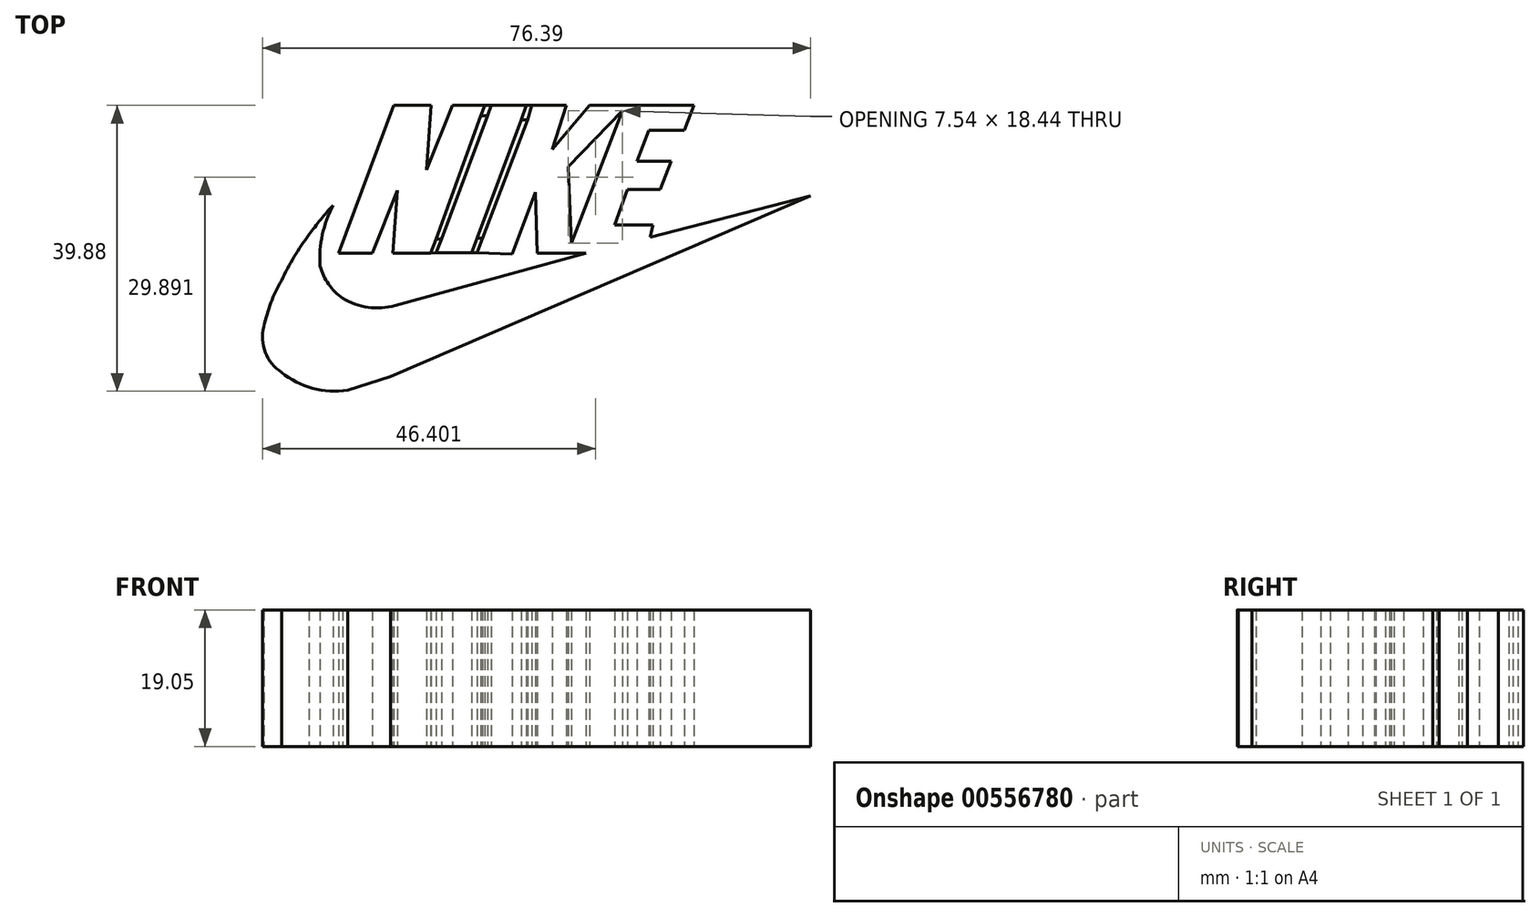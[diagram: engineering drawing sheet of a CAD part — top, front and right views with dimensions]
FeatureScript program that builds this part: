
annotation { "Feature Type Name" : "Feature", "Feature Type Description" : "" }
export const myFeature = defineFeature(function(context is Context, id is Id, definition is map)
    precondition{}
    {
        {
            var Q0;
            Q0=qCreatedBy(makeId("Top.planeOp"),FACE);
            var sketch = newSketch(context, id + "F0", { "sketchPlane" : qUnion([Q0])});
            skLineSegment(sketch, "E0", {"start": v(-58.07, 39.74) * mm, "end": v(-65.82, 19.1) * mm});
            skLineSegment(sketch, "E1", {"start": v(-65.82, 19.1) * mm, "end": v(-61.07, 19.1) * mm});
            skLineSegment(sketch, "E2", {"start": v(-61.07, 19.1) * mm, "end": v(-57.6, 27.87) * mm});
            skLineSegment(sketch, "E3", {"start": v(-57.6, 27.87) * mm, "end": v(-58.23, 19.1) * mm});
            skLineSegment(sketch, "E4", {"start": v(-58.23, 19.1) * mm, "end": v(-52.94, 19.1) * mm});
            skLineSegment(sketch, "E5", {"start": v(-45.41, 39.74) * mm, "end": v(-49.94, 39.74) * mm});
            skLineSegment(sketch, "E6", {"start": v(-49.94, 39.74) * mm, "end": v(-53.5, 30.77) * mm});
            skLineSegment(sketch, "E7", {"start": v(-53.5, 30.77) * mm, "end": v(-52.88, 39.74) * mm});
            skLineSegment(sketch, "E8", {"start": v(-52.88, 39.74) * mm, "end": v(-58.07, 39.74) * mm});
            skLineSegment(sketch, "E9", {"start": v(-44.5, 39.74) * mm, "end": v(-39.63, 39.74) * mm});
            skLineSegment(sketch, "E10", {"start": v(-52.2, 19.19) * mm, "end": v(-47.26, 19.19) * mm});
            skLineSegment(sketch, "E11", {"start": v(-38.37, 27.66) * mm, "end": v(-41.6, 18.98) * mm});
            skLineSegment(sketch, "E12", {"start": v(-41.6, 18.98) * mm, "end": v(-46.5, 19.19) * mm});
            skLineSegment(sketch, "E13", {"start": v(-38.12, 19.1) * mm, "end": v(-38.37, 27.66) * mm});
            skLineSegment(sketch, "E14", {"start": v(-31.33, 19.1) * mm, "end": v(-38.12, 19.1) * mm});
            skLineSegment(sketch, "E15", {"start": v(-31.33, 19.1) * mm, "end": v(-57.9, 11.81) * mm});
            skArc(sketch, "E16", {"start": v(-65.2, 12.82) * mm, "mid": v(-61.66, 11.57) * mm, "end": v(-57.9, 11.81) * mm});
            skArc(sketch, "E17", {"start": v(-68.38, 17.34) * mm, "mid": v(-67.18, 14.8) * mm, "end": v(-65.2, 12.82) * mm});
            skArc(sketch, "E18", {"start": v(-66.54, 25.81) * mm, "mid": v(-68.04, 21.7) * mm, "end": v(-68.38, 17.34) * mm});
            skArc(sketch, "E19", {"start": v(-66.54, 25.81) * mm, "mid": v(-68.29, 23.82) * mm, "end": v(-69.9, 21.7) * mm});
            skArc(sketch, "E20", {"start": v(-69.9, 21.7) * mm, "mid": v(-71.98, 18.61) * mm, "end": v(-73.75, 15.33) * mm});
            skArc(sketch, "E21", {"start": v(-73.75, 15.33) * mm, "mid": v(-75.23, 12.2) * mm, "end": v(-76.2, 8.88) * mm});
            skArc(sketch, "E22", {"start": v(-76.2, 8.88) * mm, "mid": v(-76, 5.3) * mm, "end": v(-73.75, 2.5) * mm});
            skArc(sketch, "E23", {"start": v(-73.75, 2.5) * mm, "mid": v(-69.4, 0.27) * mm, "end": v(-64.53, 0) * mm});
            skLineSegment(sketch, "E24", {"start": v(-64.53, 0) * mm, "end": v(-58.58, 1.92) * mm});
            skLineSegment(sketch, "E25", {"start": v(-58.58, 1.92) * mm, "end": v(0, 27.15) * mm});
            skLineSegment(sketch, "E26", {"start": v(0, 27.15) * mm, "end": v(-22.36, 21.37) * mm});
            skLineSegment(sketch, "E27", {"start": v(-21.94, 23.04) * mm, "end": v(-27.3, 23.04) * mm});
            skLineSegment(sketch, "E28", {"start": v(-27.3, 23.04) * mm, "end": v(-25.55, 28) * mm});
            skLineSegment(sketch, "E29", {"start": v(-25.55, 28) * mm, "end": v(-20.93, 28) * mm});
            skLineSegment(sketch, "E30", {"start": v(-20.93, 28) * mm, "end": v(-19.43, 31.93) * mm});
            skLineSegment(sketch, "E31", {"start": v(-19.43, 31.93) * mm, "end": v(-24.2, 31.93) * mm});
            skLineSegment(sketch, "E32", {"start": v(-24.2, 31.93) * mm, "end": v(-22.53, 36.3) * mm});
            skLineSegment(sketch, "E33", {"start": v(-22.53, 36.3) * mm, "end": v(-17.58, 36.3) * mm});
            skLineSegment(sketch, "E34", {"start": v(-17.58, 36.3) * mm, "end": v(-16.24, 39.74) * mm});
            skLineSegment(sketch, "E35", {"start": v(-16.24, 39.74) * mm, "end": v(-30.83, 39.74) * mm});
            skLineSegment(sketch, "E36", {"start": v(-30.83, 39.74) * mm, "end": v(-36.02, 33.6) * mm});
            skLineSegment(sketch, "E37", {"start": v(-30.83, 39.74) * mm, "end": v(-16.24, 39.74) * mm});
            skLineSegment(sketch, "E38", {"start": v(-36.02, 33.6) * mm, "end": v(-34.01, 39.74) * mm});
            skLineSegment(sketch, "E39", {"start": v(-34.01, 39.74) * mm, "end": v(-38.88, 39.74) * mm});
            skLineSegment(sketch, "E40", {"start": v(-33.34, 20.53) * mm, "end": v(-26.22, 38.97) * mm});
            skLineSegment(sketch, "E41", {"start": v(-26.22, 38.97) * mm, "end": v(-33.76, 31.18) * mm});
            skLineSegment(sketch, "E42", {"start": v(-33.76, 31.18) * mm, "end": v(-33.34, 20.53) * mm});
            skLineSegment(sketch, "E43", {"start": v(-21.94, 23.04) * mm, "end": v(-22.36, 21.37) * mm});
            skLineSegment(sketch, "E44", {"start": v(-38.88, 39.74) * mm, "end": v(-39.63, 39.74) * mm});
            skLineSegment(sketch, "E45", {"start": v(-45.41, 39.74) * mm, "end": v(-44.5, 39.74) * mm});
            skLineSegment(sketch, "E46", {"start": v(-39.63, 39.74) * mm, "end": v(-38.88, 39.74) * mm});
            skLineSegment(sketch, "E47", {"start": v(-46.5, 19.19) * mm, "end": v(-47.26, 19.19) * mm});
            skLineSegment(sketch, "E48", {"start": v(-52.94, 19.1) * mm, "end": v(-52.2, 19.19) * mm});
            skLineSegment(sketch, "E49", {"start": v(-46.5, 19.19) * mm, "end": v(-45.75, 21.23) * mm});
            skLineSegment(sketch, "E50", {"start": v(-45.75, 21.23) * mm, "end": v(-46.5, 21.23) * mm});
            skLineSegment(sketch, "E51", {"start": v(-46.5, 21.23) * mm, "end": v(-47.26, 19.19) * mm});
            skLineSegment(sketch, "E52", {"start": v(-52.94, 19.1) * mm, "end": v(-52.2, 21.07) * mm});
            skLineSegment(sketch, "E53", {"start": v(-52.2, 21.07) * mm, "end": v(-51.42, 21.07) * mm});
            skLineSegment(sketch, "E54", {"start": v(-51.42, 21.07) * mm, "end": v(-52.2, 19.19) * mm});
            skLineSegment(sketch, "E55", {"start": v(-45.41, 39.74) * mm, "end": v(-45.95, 38.3) * mm});
            skLineSegment(sketch, "E56", {"start": v(-45.95, 38.3) * mm, "end": v(-45.04, 38.3) * mm});
            skLineSegment(sketch, "E57", {"start": v(-45.04, 38.3) * mm, "end": v(-44.5, 39.74) * mm});
            skLineSegment(sketch, "E58", {"start": v(-39.63, 39.74) * mm, "end": v(-40.34, 37.71) * mm});
            skLineSegment(sketch, "E59", {"start": v(-39.45, 37.71) * mm, "end": v(-40.34, 37.71) * mm});
            skLineSegment(sketch, "E60", {"start": v(-39.45, 37.71) * mm, "end": v(-38.88, 39.74) * mm});
            skLineSegment(sketch, "E61", {"start": v(-45.95, 38.3) * mm, "end": v(-52.2, 21.07) * mm});
            skLineSegment(sketch, "E62", {"start": v(-40.34, 37.71) * mm, "end": v(-46.5, 21.23) * mm});
            skLineSegment(sketch, "E63", {"start": v(-51.42, 21.07) * mm, "end": v(-45.04, 38.3) * mm});
            skLineSegment(sketch, "E64", {"start": v(-39.45, 37.71) * mm, "end": v(-45.75, 21.23) * mm});
            skSolve(sketch);
        }
        {
            var Q0;
            Q0=makeQuery(id+"F0.imprint","IMPRINT",FACE,{"disambiguationData":[TD([[makeQuery(id+"F0.imprint","IMPRINT",EDGE,{"derivedFrom":sQuery(id+"F0.wireOp",EDGE,"T5yt7kch-MNiK-NvNt-go97-Sg4zb0o8OVLQ")}),1.0]])]});
            var Q1;
            Q1=makeQuery(id+"F0.imprint","IMPRINT",FACE,{"disambiguationData":[TD([[makeQuery(id+"F0.imprint","IMPRINT",EDGE,{"derivedFrom":sQuery(id+"F0.wireOp",EDGE,"E10")}),1.0]])]});
            var Q2;
            Q2=makeQuery(id+"F0.imprint","IMPRINT",FACE,{"disambiguationData":[TD([[makeQuery(id+"F0.imprint","IMPRINT",EDGE,{"derivedFrom":sQuery(id+"F0.wireOp",EDGE,"E0")}),1.0]])]});
            var Q3;
            Q3=makeQuery(id+"F0.imprint","IMPRINT",FACE,{"disambiguationData":[TD([[makeQuery(id+"F0.imprint","IMPRINT",EDGE,{"derivedFrom":sQuery(id+"F0.wireOp",EDGE,"E11")}),-1.0]])]});
            extrude(context, id + "F1", {"entities" : qUnion([Q0, Q1, Q2, Q3]), "depth" : 19.05 * mm, "offsetDistance" : 25.4 * mm});
        }
        {
            var Q0;
            Q0=qCreatedBy(makeId("Top.planeOp"),FACE);
            var sketch = newSketch(context, id + "F2", { "sketchPlane" : qUnion([Q0])});
            skLineSegment(sketch, "E65.0", {"start": v(-38.88, 39.74) * mm, "end": v(-39.63, 39.74) * mm});
            skLineSegment(sketch, "E66.0", {"start": v(-39.45, 37.71) * mm, "end": v(-40.34, 37.71) * mm});
            skLineSegment(sketch, "E67.0", {"start": v(-39.63, 39.74) * mm, "end": v(-40.34, 37.71) * mm});
            skLineSegment(sketch, "E68.0", {"start": v(-39.45, 37.71) * mm, "end": v(-38.88, 39.74) * mm});
            skLineSegment(sketch, "E69.0", {"start": v(-45.75, 21.23) * mm, "end": v(-46.5, 21.23) * mm});
            skLineSegment(sketch, "E70.0.1", {"start": v(-46.5, 21.23) * mm, "end": v(-47.26, 19.19) * mm});
            skLineSegment(sketch, "E70.0.2", {"start": v(-47.26, 19.19) * mm, "end": v(-46.5, 19.19) * mm});
            skLineSegment(sketch, "E70.0.3", {"start": v(-46.5, 19.19) * mm, "end": v(-45.75, 21.23) * mm});
            skLineSegment(sketch, "E71.0.0", {"start": v(-51.42, 21.07) * mm, "end": v(-52.2, 21.07) * mm});
            skLineSegment(sketch, "E71.0.1", {"start": v(-52.2, 21.07) * mm, "end": v(-52.94, 19.1) * mm});
            skLineSegment(sketch, "E71.0.2", {"start": v(-52.94, 19.1) * mm, "end": v(-52.2, 19.19) * mm});
            skLineSegment(sketch, "E71.0.3", {"start": v(-52.2, 19.19) * mm, "end": v(-51.42, 21.07) * mm});
            skLineSegment(sketch, "E72.0.0", {"start": v(-44.5, 39.74) * mm, "end": v(-45.41, 39.74) * mm});
            skLineSegment(sketch, "E72.0.1", {"start": v(-45.41, 39.74) * mm, "end": v(-45.95, 38.3) * mm});
            skLineSegment(sketch, "E72.0.2", {"start": v(-45.95, 38.3) * mm, "end": v(-45.04, 38.3) * mm});
            skLineSegment(sketch, "E72.0.3", {"start": v(-45.04, 38.3) * mm, "end": v(-44.5, 39.74) * mm});
            skSolve(sketch);
        }
        {
            var Q0;
            Q0 = qSketchRegion(id + "F2", true);
            var Q1;
            Q1=makeQuery(id+"F1.opExtrude","CAP_FACE",FACE,{"disambiguationData":[OSD([sQuery(id+"F0.wireOp",EDGE,"E0"),sQuery(id+"F0.wireOp",EDGE,"E1"),sQuery(id+"F0.wireOp",EDGE,"E2"),sQuery(id+"F0.wireOp",EDGE,"E3"),sQuery(id+"F0.wireOp",EDGE,"E4"),sQuery(id+"F0.wireOp",EDGE,"E5"),sQuery(id+"F0.wireOp",EDGE,"E6"),sQuery(id+"F0.wireOp",EDGE,"E7"),sQuery(id+"F0.wireOp",EDGE,"E8"),sQuery(id+"F0.wireOp",EDGE,"E52"),sQuery(id+"F0.wireOp",EDGE,"E55"),sQuery(id+"F0.wireOp",EDGE,"E61")])],"isStart":false});
            extrude(context, id + "F3", {"entities" : qUnion([Q0]), "endBound" : BoundingType.UP_TO_SURFACE, "depth" : 25.4 * mm, "endBoundEntityFace" : qUnion([Q1]), "offsetDistance" : 25.4 * mm});
        }
    });
